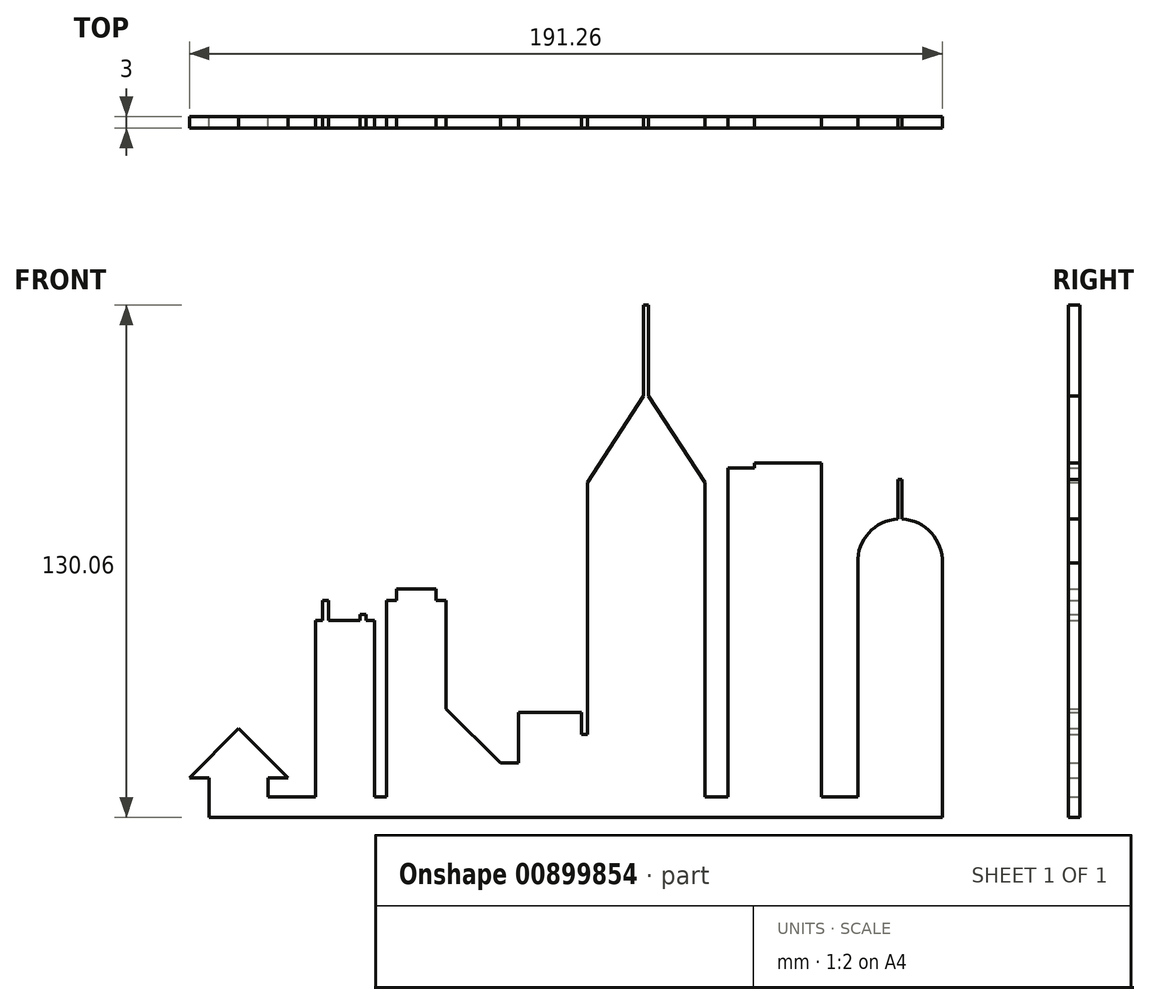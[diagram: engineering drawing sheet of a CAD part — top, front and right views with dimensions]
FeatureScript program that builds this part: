
annotation { "Feature Type Name" : "Feature", "Feature Type Description" : "" }
export const myFeature = defineFeature(function(context is Context, id is Id, definition is map)
    precondition{}
    {
        {
            var Q0;
            Q0=qCreatedBy(makeId("Front.planeOp"),FACE);
            var sketch = newSketch(context, id + "F0", { "sketchPlane" : qUnion([Q0])});
            skLineSegment(sketch, "E0", {"start": v(-94.98, -43) * mm, "end": v(105.02, -43) * mm});
            skLineSegment(sketch, "E1", {"start": v(105.02, -43) * mm, "end": v(105.02, 157) * mm});
            skLineSegment(sketch, "E2", {"start": v(-94.98, -43) * mm, "end": v(-94.98, 157) * mm});
            skLineSegment(sketch, "E3", {"start": v(-85.98, -43) * mm, "end": v(-85.98, -33) * mm});
            skLineSegment(sketch, "E4", {"start": v(-85.98, -33) * mm, "end": v(-90.98, -33) * mm});
            skLineSegment(sketch, "E5", {"start": v(-70.98, -43) * mm, "end": v(-70.98, -33) * mm});
            skLineSegment(sketch, "E6", {"start": v(-70.98, -33) * mm, "end": v(-65.98, -33) * mm});
            skLineSegment(sketch, "E7", {"start": v(-90.98, -33) * mm, "end": v(-78.48, -20.5) * mm});
            skLineSegment(sketch, "E8", {"start": v(-65.98, -33) * mm, "end": v(-78.48, -20.5) * mm});
            skLineSegment(sketch, "E9", {"start": v(-58.92, -43) * mm, "end": v(-58.92, 7) * mm});
            skLineSegment(sketch, "E10", {"start": v(-58.92, 7) * mm, "end": v(-43.92, 7) * mm});
            skLineSegment(sketch, "E11", {"start": v(-43.92, 7) * mm, "end": v(-43.92, -43) * mm});
            skLineSegment(sketch, "E12.bottom", {"start": v(-57.18, 7) * mm, "end": v(-55.68, 7) * mm});
            skLineSegment(sketch, "E12.top", {"start": v(-57.18, 12) * mm, "end": v(-55.68, 12) * mm});
            skLineSegment(sketch, "E12.left", {"start": v(-57.18, 7) * mm, "end": v(-57.18, 12) * mm});
            skLineSegment(sketch, "E12.right", {"start": v(-55.68, 7) * mm, "end": v(-55.68, 12) * mm});
            skLineSegment(sketch, "E13.bottom", {"start": v(-47.66, 7) * mm, "end": v(-46.16, 7) * mm});
            skLineSegment(sketch, "E13.top", {"start": v(-47.66, 8.5) * mm, "end": v(-46.16, 8.5) * mm});
            skLineSegment(sketch, "E13.left", {"start": v(-47.66, 7) * mm, "end": v(-47.66, 8.5) * mm});
            skLineSegment(sketch, "E13.right", {"start": v(-46.16, 7) * mm, "end": v(-46.16, 8.5) * mm});
            skLineSegment(sketch, "E14.bottom", {"start": v(-40.84, -43) * mm, "end": v(-25.84, -43) * mm});
            skLineSegment(sketch, "E14.top", {"start": v(-40.84, 12) * mm, "end": v(-25.84, 12) * mm});
            skLineSegment(sketch, "E14.left", {"start": v(-40.84, -43) * mm, "end": v(-40.84, 12) * mm});
            skLineSegment(sketch, "E14.right", {"start": v(-25.84, -43) * mm, "end": v(-25.84, 12) * mm});
            skLineSegment(sketch, "E15.bottom", {"start": v(-38.34, 12) * mm, "end": v(-28.34, 12) * mm});
            skLineSegment(sketch, "E15.top", {"start": v(-38.34, 15) * mm, "end": v(-28.34, 15) * mm});
            skLineSegment(sketch, "E15.left", {"start": v(-38.34, 12) * mm, "end": v(-38.34, 15) * mm});
            skLineSegment(sketch, "E15.right", {"start": v(-28.34, 12) * mm, "end": v(-28.34, 15) * mm});
            skLineSegment(sketch, "E16", {"start": v(-25.84, -15.5) * mm, "end": v(-11.93, -29.2) * mm});
            skLineSegment(sketch, "E17", {"start": v(-11.93, -29.2) * mm, "end": v(-7.41, -29.2) * mm});
            skLineSegment(sketch, "E18", {"start": v(-7.41, -29.2) * mm, "end": v(-7.41, -16.33) * mm});
            skLineSegment(sketch, "E19", {"start": v(-7.41, -16.33) * mm, "end": v(8.61, -16.33) * mm});
            skLineSegment(sketch, "E20", {"start": v(8.61, -16.33) * mm, "end": v(8.61, -21.97) * mm});
            skLineSegment(sketch, "E21", {"start": v(8.61, -21.97) * mm, "end": v(10.11, -21.97) * mm});
            skLineSegment(sketch, "E22", {"start": v(40, -43) * mm, "end": v(45.86, -43) * mm});
            skLineSegment(sketch, "E23", {"start": v(45.86, -43) * mm, "end": v(45.86, 45.75) * mm});
            skLineSegment(sketch, "E24", {"start": v(45.86, 45.75) * mm, "end": v(52.63, 45.75) * mm});
            skLineSegment(sketch, "E25", {"start": v(52.63, 47) * mm, "end": v(52.63, 45.75) * mm});
            skLineSegment(sketch, "E26", {"start": v(52.63, 47) * mm, "end": v(69.57, 47) * mm});
            skLineSegment(sketch, "E27", {"start": v(69.57, 47) * mm, "end": v(69.57, -43) * mm});
            skLineSegment(sketch, "E28", {"start": v(69.57, -43) * mm, "end": v(78.82, -43) * mm});
            skLineSegment(sketch, "E29", {"start": v(78.82, -43) * mm, "end": v(78.82, 22.5) * mm});
            skLineSegment(sketch, "E30", {"start": v(100.27, -43) * mm, "end": v(100.27, 22.5) * mm});
            skArc(sketch, "E31", {"start": v(100.27, 21.53) * mm, "mid": v(89.54, 32.75) * mm, "end": v(78.82, 21.53) * mm});
            skLineSegment(sketch, "E32", {"start": v(40, -43) * mm, "end": v(40, 42) * mm});
            skLineSegment(sketch, "E33", {"start": v(40, 42) * mm, "end": v(10.11, 42) * mm});
            skLineSegment(sketch, "E34", {"start": v(10.11, 42) * mm, "end": v(10.11, -21.97) * mm});
            skLineSegment(sketch, "E35", {"start": v(10.11, 42) * mm, "end": v(25.05, 64.98) * mm});
            skPoint(sketch, "E35.endSnap0", {"position": v(25.05, 42) * mm});
            skLineSegment(sketch, "E36", {"start": v(25.05, 64.98) * mm, "end": v(40, 42) * mm});
            skLineSegment(sketch, "E37", {"start": v(25.05, 42) * mm, "end": v(25.05, 87.06) * mm});
            skLineSegment(sketch, "E38", {"start": v(89.04, 32.74) * mm, "end": v(89.04, 42.75) * mm});
            skLineSegment(sketch, "E39", {"start": v(90.04, 32.74) * mm, "end": v(90.04, 42.75) * mm});
            skLineSegment(sketch, "E40", {"start": v(89.04, 42.75) * mm, "end": v(90.04, 42.75) * mm});
            skLineSegment(sketch, "E41", {"start": v(24.4, 63.96) * mm, "end": v(24.4, 87.06) * mm});
            skPoint(sketch, "E42.startSnap0", {"position": v(25.05, 64.53) * mm});
            skLineSegment(sketch, "E43", {"start": v(25.65, 64.06) * mm, "end": v(25.65, 87.06) * mm});
            skLineSegment(sketch, "E44", {"start": v(24.4, 87.06) * mm, "end": v(25.65, 87.06) * mm});
            skLineSegment(sketch, "E45", {"start": v(40, -37.87) * mm, "end": v(45.86, -37.87) * mm});
            skLineSegment(sketch, "E46", {"start": v(69.57, -37.87) * mm, "end": v(78.82, -37.87) * mm});
            skLineSegment(sketch, "E47", {"start": v(-40.84, -37.87) * mm, "end": v(-43.92, -37.87) * mm});
            skLineSegment(sketch, "E48", {"start": v(-58.92, -37.87) * mm, "end": v(-70.98, -37.87) * mm});
            skSolve(sketch);
        }
        {
            var Q0;
            Q0 = qSketchRegion(id + "F0", true);
            extrude(context, id + "F1", {"entities" : qUnion([Q0]), "depth" : 3 * mm, "offsetDistance" : 25 * mm});
        }
    });
